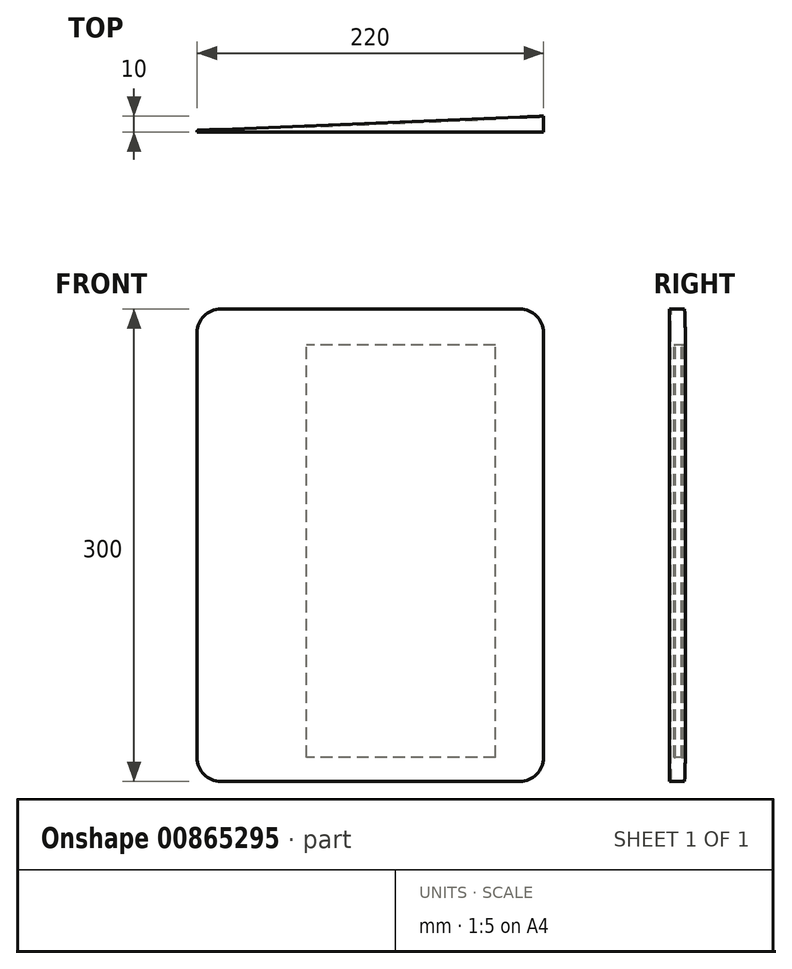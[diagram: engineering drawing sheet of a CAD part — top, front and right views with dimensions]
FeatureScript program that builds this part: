
annotation { "Feature Type Name" : "Feature", "Feature Type Description" : "" }
export const myFeature = defineFeature(function(context is Context, id is Id, definition is map)
    precondition{}
    {
        {
            var Q0;
            Q0=qCreatedBy(makeId("Top.planeOp"),FACE);
            var sketch = newSketch(context, id + "F0", { "sketchPlane" : qUnion([Q0])});
            skLineSegment(sketch, "E0", {"start": v(-103.39, -29.08) * mm, "end": v(116.61, -29.08) * mm});
            skLineSegment(sketch, "E1", {"start": v(116.61, -29.08) * mm, "end": v(116.61, -19.08) * mm});
            skLineSegment(sketch, "E2", {"start": v(116.61, -19.08) * mm, "end": v(-103.39, -28.08) * mm});
            skLineSegment(sketch, "E3", {"start": v(-103.39, -28.08) * mm, "end": v(-103.39, -29.08) * mm});
            skSolve(sketch);
        }
        {
            var Q0;
            Q0=makeQuery(id+"F0.imprint","IMPRINT",FACE,{"disambiguationData":[TD([[makeQuery(id+"F0.imprint","IMPRINT",EDGE,{"derivedFrom":sQuery(id+"F0.wireOp",EDGE,"E0")}),1.0]])]});
            var sketch = newSketch(context, id + "F1", { "sketchPlane" : qUnion([Q0])});
            skSolve(sketch);
        }
        {
            var Q0;
            Q0=makeQuery(id+"F0.imprint","IMPRINT",FACE,{"disambiguationData":[TD([[makeQuery(id+"F0.imprint","IMPRINT",EDGE,{"derivedFrom":sQuery(id+"F0.wireOp",EDGE,"E0")}),1.0]])]});
            var sketch = newSketch(context, id + "F2", { "sketchPlane" : qUnion([Q0])});
            skSolve(sketch);
        }
        {
            var Q0;
            Q0 = qSketchRegion(id + "F2", true);
            var Q1;
            Q1=makeQuery(id+"F1.imprint","IMPRINT",FACE,{"disambiguationData":[TD([[makeQuery(id+"F1.imprint","IMPRINT",EDGE,{"derivedFrom":makeQuery(id+"F0.imprint","IMPRINT",EDGE,{"derivedFrom":sQuery(id+"F0.wireOp",EDGE,"E0")})}),1.0]])]});
            extrude(context, id + "F3", {"entities" : qUnion([Q0, Q1]), "oppositeDirection" : true, "depth" : 300 * mm, "offsetDistance" : 25 * mm});
        }
        {
            var Q0;
            Q0=makeQuery(id+"F3.opExtrude","CAP_EDGE",EDGE,{"disambiguationData":[OSD([sQuery(id+"F0.wireOp",EDGE,"E3")])],"isStart":true});
            fillet(context, id + "F4", {"entities" : qUnion([Q0]), "radius" : 15 * mm, "tangentPropagation" : true, "allowEdgeOverflow" : false});
        }
        {
            var Q0;
            Q0=makeQuery(id+"F3.opExtrude","CAP_EDGE",EDGE,{"disambiguationData":[OSD([sQuery(id+"F0.wireOp",EDGE,"E3")])],"isStart":false});
            fillet(context, id + "F5", {"entities" : qUnion([Q0]), "radius" : 15 * mm, "tangentPropagation" : true, "allowEdgeOverflow" : false});
        }
        {
            var Q0;
            Q0=makeQuery(id+"F3.opExtrude","CAP_EDGE",EDGE,{"disambiguationData":[OSD([sQuery(id+"F0.wireOp",EDGE,"E1")])],"isStart":false});
            fillet(context, id + "F6", {"entities" : qUnion([Q0]), "radius" : 15 * mm, "tangentPropagation" : true, "allowEdgeOverflow" : false});
        }
        {
            var Q0;
            Q0=makeQuery(id+"F3.opExtrude","CAP_EDGE",EDGE,{"disambiguationData":[OSD([sQuery(id+"F0.wireOp",EDGE,"E1")])],"isStart":true});
            fillet(context, id + "F7", {"entities" : qUnion([Q0]), "radius" : 15 * mm, "tangentPropagation" : true, "allowEdgeOverflow" : false});
        }
        {
            var Q0;
            Q0=makeQuery(id+"F3.opExtrude","SWEPT_FACE",FACE,{"disambiguationData":[OSD([sQuery(id+"F0.wireOp",EDGE,"E2")])]});
            var sketch = newSketch(context, id + "F8", { "sketchPlane" : qUnion([Q0])});
            skLineSegment(sketch, "E4.bottom", {"start": v(-85.15, -284.73) * mm, "end": v(35.02, -284.73) * mm});
            skLineSegment(sketch, "E4.top", {"start": v(-85.15, -22.8) * mm, "end": v(35.02, -22.8) * mm});
            skLineSegment(sketch, "E4.left", {"start": v(-85.15, -284.73) * mm, "end": v(-85.15, -22.8) * mm});
            skLineSegment(sketch, "E4.right", {"start": v(35.02, -284.73) * mm, "end": v(35.02, -22.8) * mm});
            skSolve(sketch);
        }
        {
            var Q0;
            Q0 = qSketchRegion(id + "F8", true);
            extrude(context, id + "F9", {"entities" : qUnion([Q0]), "operationType" : NewBodyOperationType.REMOVE, "oppositeDirection" : true, "depth" : 1 * mm, "offsetDistance" : 25 * mm});
        }
    });
